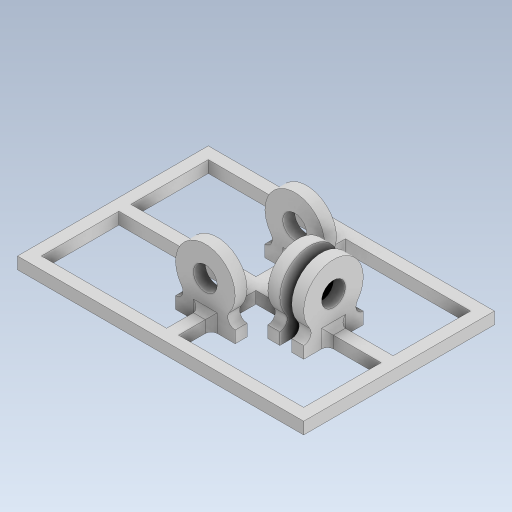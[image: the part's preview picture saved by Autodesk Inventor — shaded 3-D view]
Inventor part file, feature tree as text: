
AUTODESK INVENTOR PART (.ipt)
format: ipt  version: 2023 (Build 270158000, 158)  size: 286,208 bytes
history: native  units: in
note: dims shown in document units (in); Inventor stores cm internally (conversion verified against a paired STEP export)
features: extrude x3, sketch x3, mirror x1, pattern_linear x1, fillet x1
ambient origin geometry x8: Origin, YZ Plane, XZ Plane, XY Plane, X Axis, Y Axis, Z Axis, Center Point
bodies: Solid1 (feature_tree)
feature tree (9):
  extrude  "Extrusion1"  Depth=0.25in
  extrude  "Extrusion2"  Depth=0.25in
  mirror  "Mirror1"
  extrude  "Extrusion3"  Depth=4.0in
  pattern_linear  "Rectangular Pattern1"  Spacing1=6.0in  [1 undecoded]
  fillet  "Fillet1"  Radius=0.25in
  sketch  "Sketch1"  dims[d0=0.25in d1=0.25in]
  sketch  "Sketch2"  dims[d2=0.25in d3=0.25in]
  sketch  "Sketch3"  dims[d4=0.25in d5=4.0in d6=6.0in d7=0.25in d8=1.25in d9=0.25in d10=0.25in d11=0.0in d12=1.0in d13=0.5in d14=0.5in d15=1.25in d16=1.25in d17=0.25in d18=0.0in d20=0.5in d22=1.25in d23=1.25in d24=0.0in d25=0.0in d26=0.7874in d28=0.5in d29=0.125in d27=0.0344in]
note: 1 required parameter value undecoded (feature->parameter linkage not recoverable at this tier; creation-order binding heuristic only, values carry confidence <= 0.55)
